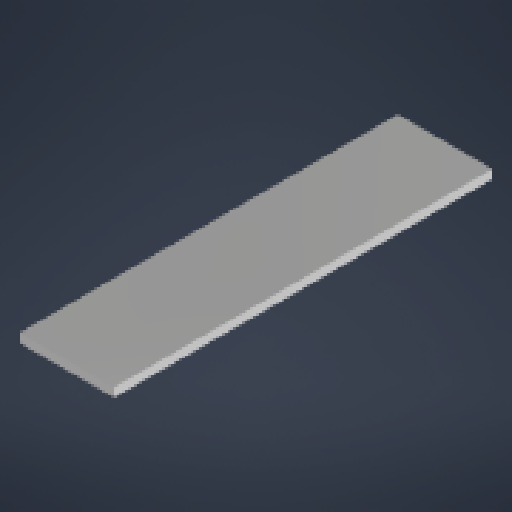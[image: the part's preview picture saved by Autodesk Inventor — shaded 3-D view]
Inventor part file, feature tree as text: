
AUTODESK INVENTOR PART (.ipt)
format: ipt  version: 2024 (Build 280153000, 153)  size: 121,344 bytes
history: native  units: mm
features: other x1, extrude x1, sketch x1
ambient origin geometry x8: Origin, YZ Plane, XZ Plane, XY Plane, X Axis, Y Axis, Z Axis, Center Point
bodies: Body1 (feature_tree)
feature tree (3):
  other  "솔리드1"
  extrude  "돌출1"  Depth=32.0mm
  sketch  "스케치1"
